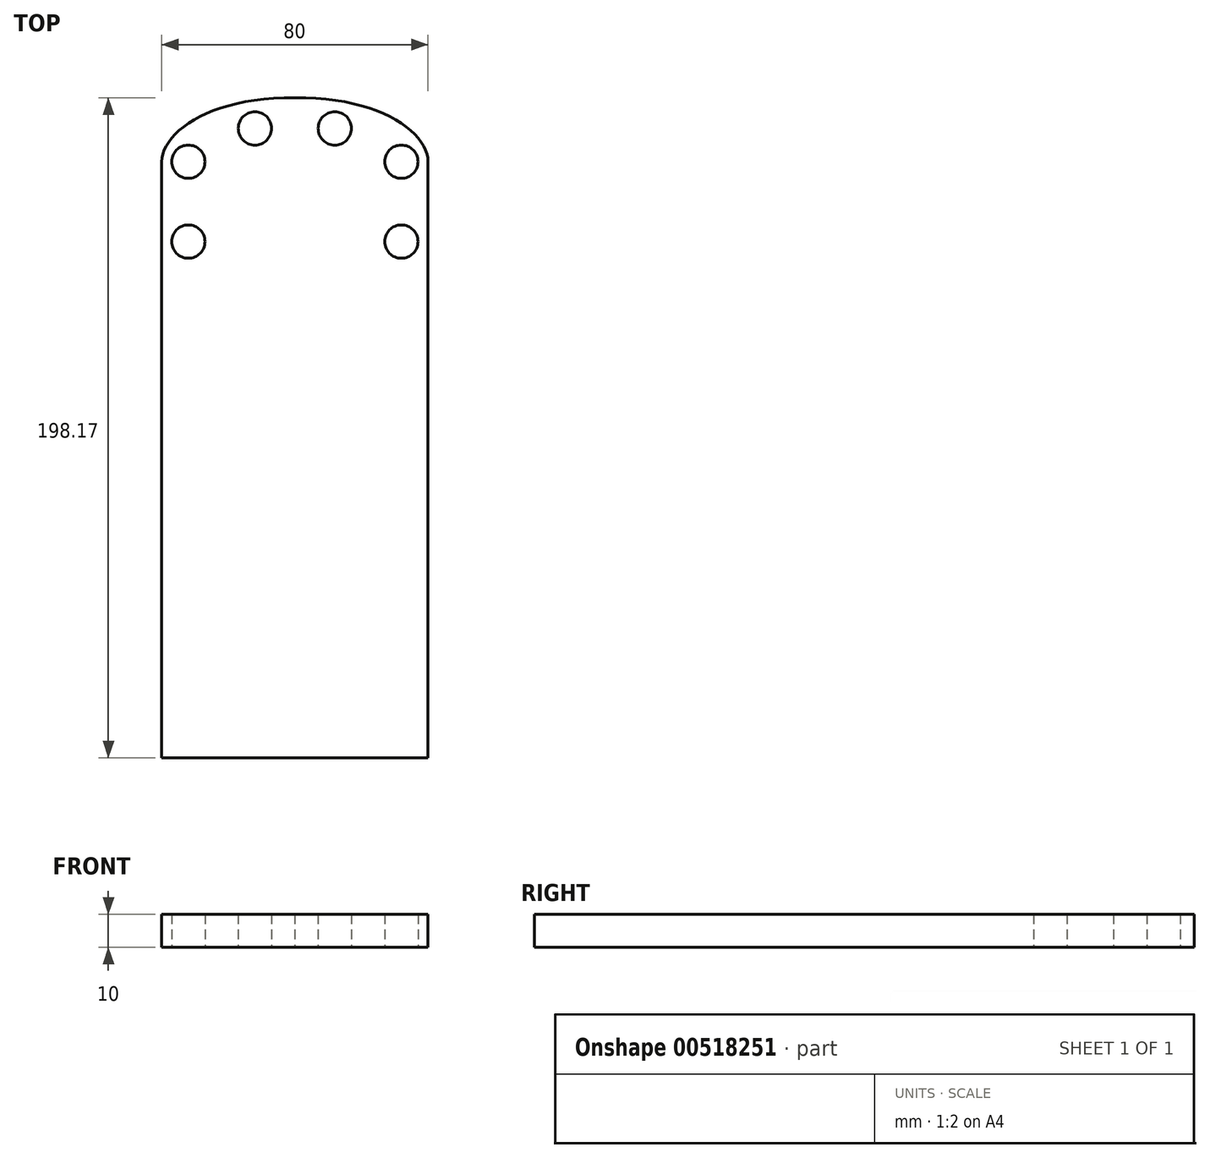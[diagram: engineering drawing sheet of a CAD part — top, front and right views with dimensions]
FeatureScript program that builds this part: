
annotation { "Feature Type Name" : "Feature", "Feature Type Description" : "" }
export const myFeature = defineFeature(function(context is Context, id is Id, definition is map)
    precondition{}
    {
        {
            var Q0;
            Q0=qCreatedBy(makeId("Top.planeOp"),FACE);
            var sketch = newSketch(context, id + "F0", { "sketchPlane" : qUnion([Q0])});
            skLineSegment(sketch, "E0.bottom", {"start": v(0, 0) * mm, "end": v(80, 0) * mm});
            skLineSegment(sketch, "E0.left", {"start": v(0, 0) * mm, "end": v(0, 179) * mm});
            skLineSegment(sketch, "E0.right", {"start": v(80, 0) * mm, "end": v(80, 179) * mm});
            skPoint(sketch, "E1", {"position": v(40, 200) * mm});
            skPoint(sketch, "E2", {"position": v(40, 0) * mm});
            skLineSegment(sketch, "E3", {"start": v(40, 198.16) * mm, "end": v(40, 0) * mm, "construction": true});
            skCircle(sketch, "E4", {"center": v(52, 189) * mm, "radius": 5 * mm});
            skCircle(sketch, "E5", {"center": v(72, 179) * mm, "radius": 5 * mm});
            skCircle(sketch, "E6", {"center": v(72, 155) * mm, "radius": 5 * mm});
            skCircle(sketch, "E7.MirrorC", {"center": v(28, 189) * mm, "radius": 5 * mm});
            skCircle(sketch, "E8.MirrorC", {"center": v(8, 179) * mm, "radius": 5 * mm});
            skCircle(sketch, "E9.MirrorC", {"center": v(8, 155) * mm, "radius": 5 * mm});
            skFitSpline(sketch, "E10", {"points": [v(80, 179) * mm, v(40, 198.16) * mm], "startDerivative": vector(0, 26.44) * mm, "endDerivative": vector(-75.53, -1.44) * mm});
            skFitSpline(sketch, "E11.MirrorCS", {"points": [v(0, 179) * mm, v(40, 198.16) * mm], "startDerivative": vector(0, 26.44) * mm, "endDerivative": vector(75.53, -1.44) * mm});
            skPoint(sketch, "E12.orphan", {"position": v(0, 200) * mm});
            skPoint(sketch, "E0.top.end.orphan", {"position": v(80, 200) * mm});
            skSolve(sketch);
        }
        {
            var Q0;
            Q0 = qSketchRegion(id + "F0", true);
            extrude(context, id + "F1", {"entities" : qUnion([Q0]), "depth" : 10 * mm, "offsetDistance" : 25 * mm});
        }
    });
